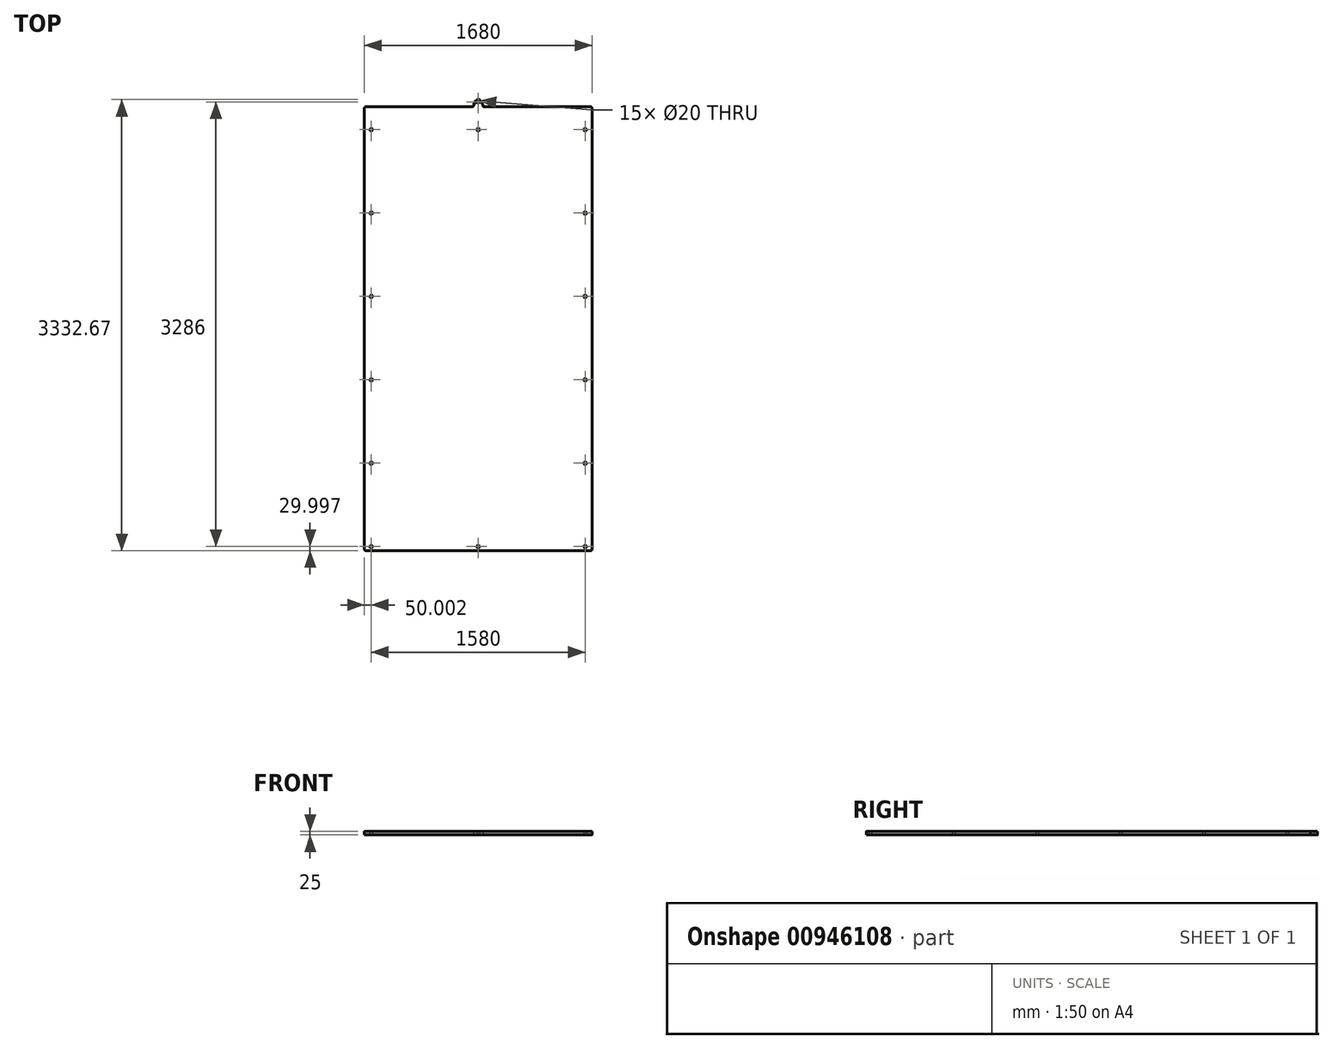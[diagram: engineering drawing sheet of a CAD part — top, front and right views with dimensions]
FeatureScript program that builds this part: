
annotation { "Feature Type Name" : "Feature", "Feature Type Description" : "" }
export const myFeature = defineFeature(function(context is Context, id is Id, definition is map)
    precondition{}
    {
        {
            var Q0;
            Q0=qCreatedBy(makeId("Top.planeOp"),FACE);
            var sketch = newSketch(context, id + "F0", { "sketchPlane" : qUnion([Q0])});
            skLineSegment(sketch, "E0.bottom", {"start": v(784.18, 2003.67) * mm, "end": v(-4.82, 2003.67) * mm});
            skLineSegment(sketch, "E0.top", {"start": v(784.18, -1276.33) * mm, "end": v(-875.82, -1276.33) * mm});
            skLineSegment(sketch, "E0.left", {"start": v(794.18, 1993.67) * mm, "end": v(794.18, -1266.33) * mm});
            skLineSegment(sketch, "E0.right", {"start": v(-885.82, 1993.67) * mm, "end": v(-885.82, -1266.33) * mm});
            skCircle(sketch, "E1", {"center": v(-45.82, -1246.33) * mm, "radius": 10 * mm});
            skPoint(sketch, "E1.centerSnap0", {"position": v(-45.82, -1276.33) * mm});
            skCircle(sketch, "E2", {"center": v(744.18, -1246.33) * mm, "radius": 10 * mm});
            skCircle(sketch, "E3", {"center": v(-835.82, -1246.33) * mm, "radius": 10 * mm});
            skCircle(sketch, "E4", {"center": v(-835.82, -630.33) * mm, "radius": 10 * mm});
            skCircle(sketch, "E5", {"center": v(-835.82, -14.33) * mm, "radius": 10 * mm});
            skCircle(sketch, "E6", {"center": v(-835.82, 601.67) * mm, "radius": 10 * mm});
            skCircle(sketch, "E7", {"center": v(-835.82, 1217.67) * mm, "radius": 10 * mm});
            skCircle(sketch, "E8", {"center": v(-835.82, 1833.67) * mm, "radius": 10 * mm});
            skCircle(sketch, "E9", {"center": v(744.18, -630.33) * mm, "radius": 10 * mm});
            skCircle(sketch, "E10", {"center": v(744.18, -14.33) * mm, "radius": 10 * mm});
            skCircle(sketch, "E11", {"center": v(744.18, 601.67) * mm, "radius": 10 * mm});
            skCircle(sketch, "E12", {"center": v(744.18, 1217.67) * mm, "radius": 10 * mm});
            skCircle(sketch, "E13", {"center": v(744.18, 1833.67) * mm, "radius": 10 * mm});
            skCircle(sketch, "E14", {"center": v(-45.82, 1833.67) * mm, "radius": 10 * mm});
            skPoint(sketch, "E14.centerSnap0", {"position": v(-45.82, 2003.67) * mm});
            skCircle(sketch, "E15", {"center": v(-45.82, 2039.67) * mm, "radius": 10 * mm});
            skLineSegment(sketch, "E16", {"start": v(-81.82, 2008.67) * mm, "end": v(-81.82, 2011.01) * mm});
            skLineSegment(sketch, "E17", {"start": v(-80.5, 2015.97) * mm, "end": v(-63.18, 2046.26) * mm});
            skLineSegment(sketch, "E18", {"start": v(-28.46, 2046.26) * mm, "end": v(-11.14, 2015.97) * mm});
            skLineSegment(sketch, "E19", {"start": v(-9.82, 2011.01) * mm, "end": v(-9.82, 2008.67) * mm});
            skPoint(sketch, "E20.visualSharp", {"position": v(-45.82, 2076.63) * mm});
            skArc(sketch, "E20.filletArc", {"start": v(-28.46, 2046.26) * mm, "mid": v(-45.82, 2056.34) * mm, "end": v(-63.18, 2046.26) * mm});
            skPoint(sketch, "E21.visualSharp", {"position": v(-81.82, 2013.67) * mm});
            skArc(sketch, "E21.filletArc", {"start": v(-80.5, 2015.97) * mm, "mid": v(-81.48, 2013.58) * mm, "end": v(-81.82, 2011.01) * mm});
            skPoint(sketch, "E22.visualSharp", {"position": v(-9.82, 2013.67) * mm});
            skArc(sketch, "E22.filletArc", {"start": v(-9.82, 2011.01) * mm, "mid": v(-10.15, 2013.58) * mm, "end": v(-11.14, 2015.97) * mm});
            skPoint(sketch, "E23", {"position": v(-91.82, 2013.67) * mm});
            skPoint(sketch, "E24", {"position": v(-86.82, 2008.67) * mm});
            skArc(sketch, "E25", {"start": v(-86.82, 2003.67) * mm, "mid": v(-83.28, 2005.13) * mm, "end": v(-81.82, 2008.67) * mm});
            skPoint(sketch, "E26.orphan", {"position": v(-81.82, 2003.67) * mm});
            skLineSegment(sketch, "E27.trimOffspring", {"start": v(-86.82, 2003.67) * mm, "end": v(-875.82, 2003.67) * mm});
            skPoint(sketch, "E28", {"position": v(0.18, 2013.67) * mm});
            skPoint(sketch, "E29", {"position": v(-4.82, 2008.67) * mm});
            skArc(sketch, "E30", {"start": v(-9.82, 2008.67) * mm, "mid": v(-8.35, 2005.13) * mm, "end": v(-4.82, 2003.67) * mm});
            skPoint(sketch, "E31.orphan", {"position": v(-9.82, 2003.67) * mm});
            skLineSegment(sketch, "E32.trimOffspring", {"start": v(-45.82, 2003.67) * mm, "end": v(-81.82, 2003.67) * mm});
            skPoint(sketch, "E33.visualSharp", {"position": v(-885.82, 2003.67) * mm});
            skArc(sketch, "E33.filletArc", {"start": v(-875.82, 2003.67) * mm, "mid": v(-882.89, 2000.74) * mm, "end": v(-885.82, 1993.67) * mm});
            skPoint(sketch, "E34.visualSharp", {"position": v(794.18, 2003.67) * mm});
            skArc(sketch, "E34.filletArc", {"start": v(794.18, 1993.67) * mm, "mid": v(791.25, 2000.74) * mm, "end": v(784.18, 2003.67) * mm});
            skPoint(sketch, "E35.visualSharp", {"position": v(794.18, -1276.33) * mm});
            skArc(sketch, "E35.filletArc", {"start": v(784.18, -1276.33) * mm, "mid": v(791.25, -1273.4) * mm, "end": v(794.18, -1266.33) * mm});
            skPoint(sketch, "E36.visualSharp", {"position": v(-885.82, -1276.33) * mm});
            skArc(sketch, "E36.filletArc", {"start": v(-885.82, -1266.33) * mm, "mid": v(-882.89, -1273.4) * mm, "end": v(-875.82, -1276.33) * mm});
            skSolve(sketch);
        }
        {
            var Q0;
            Q0 = qSketchRegion(id + "F0", true);
            extrude(context, id + "F1", {"entities" : qUnion([Q0]), "depth" : 25 * mm, "offsetDistance" : 25 * mm});
        }
    });
